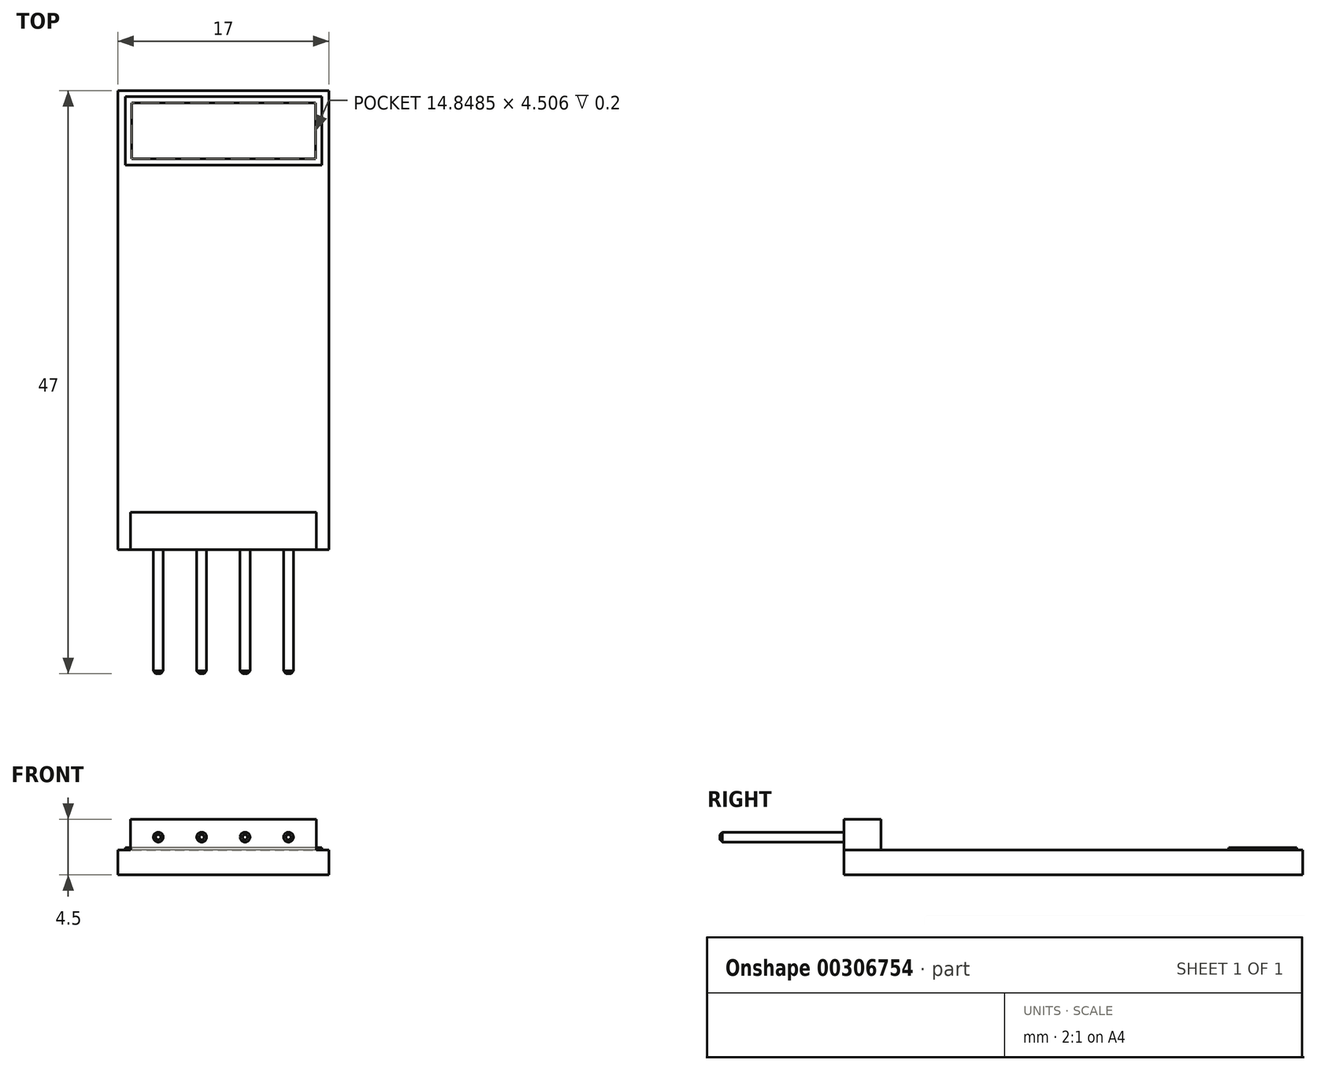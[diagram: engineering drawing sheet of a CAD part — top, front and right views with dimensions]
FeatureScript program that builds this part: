
annotation { "Feature Type Name" : "Feature", "Feature Type Description" : "" }
export const myFeature = defineFeature(function(context is Context, id is Id, definition is map)
    precondition{}
    {
        {
            var Q0;
            Q0=qCreatedBy(makeId("Top.planeOp"),FACE);
            var sketch = newSketch(context, id + "F0", { "sketchPlane" : qUnion([Q0])});
            skLineSegment(sketch, "E0.bottom", {"start": v(-8.5, 18.5) * mm, "end": v(8.5, 18.5) * mm});
            skLineSegment(sketch, "E0.top", {"start": v(-8.5, -18.5) * mm, "end": v(8.5, -18.5) * mm});
            skLineSegment(sketch, "E0.left", {"start": v(-8.5, 18.5) * mm, "end": v(-8.5, -18.5) * mm});
            skLineSegment(sketch, "E0.right", {"start": v(8.5, 18.5) * mm, "end": v(8.5, -18.5) * mm});
            skSolve(sketch);
        }
        {
            var Q0;
            Q0=makeQuery(id+"F0.imprint","IMPRINT",FACE,{"disambiguationData":[TD([[makeQuery(id+"F0.imprint","IMPRINT",EDGE,{"derivedFrom":sQuery(id+"F0.wireOp",EDGE,"E0.bottom")}),-1.0]])]});
            extrude(context, id + "F1", {"entities" : qUnion([Q0]), "depth" : 2 * mm, "symmetric" : true});
        }
        {
            var Q0;
            Q0=makeQuery(id+"F1.opExtrude","CAP_FACE",FACE,{"disambiguationData":[OSD([sQuery(id+"F0.wireOp",EDGE,"E0.bottom"),sQuery(id+"F0.wireOp",EDGE,"E0.top"),sQuery(id+"F0.wireOp",EDGE,"E0.left"),sQuery(id+"F0.wireOp",EDGE,"E0.right")])],"isStart":false});
            var sketch = newSketch(context, id + "F2", { "sketchPlane" : qUnion([Q0])});
            skLineSegment(sketch, "E1.bottom", {"start": v(-7.5, -18.5) * mm, "end": v(7.5, -18.5) * mm});
            skLineSegment(sketch, "E1.top", {"start": v(-7.5, -15.5) * mm, "end": v(7.5, -15.5) * mm});
            skLineSegment(sketch, "E1.left", {"start": v(-7.5, -18.5) * mm, "end": v(-7.5, -15.5) * mm});
            skLineSegment(sketch, "E1.right", {"start": v(7.5, -18.5) * mm, "end": v(7.5, -15.5) * mm});
            skSolve(sketch);
        }
        {
            var Q0;
            Q0=makeQuery(id+"F2.imprint","IMPRINT",FACE,{"disambiguationData":[TD([[makeQuery(id+"F2.imprint","IMPRINT",EDGE,{"derivedFrom":sQuery(id+"F2.wireOp",EDGE,"E1.bottom")}),1.0]])]});
            extrude(context, id + "F3", {"entities" : qUnion([Q0]), "operationType" : NewBodyOperationType.ADD, "depth" : 2.5 * mm});
        }
        {
            var Q0;
            Q0=makeQuery(id+"F3.boolean.opBoolean","MERGE",FACE,{"derivedFrom":[makeQuery(id+"F1.opExtrude","SWEPT_FACE",FACE,{"disambiguationData":[OSD([sQuery(id+"F0.wireOp",EDGE,"E0.top")])]}),makeQuery(id+"F3.opExtrude","SWEPT_FACE",FACE,{"disambiguationData":[OSD([sQuery(id+"F2.wireOp",EDGE,"E1.bottom")])]})]});
            var sketch = newSketch(context, id + "F4", { "sketchPlane" : qUnion([Q0])});
            skCircle(sketch, "E2", {"center": v(-5.25, 2.05) * mm, "radius": 0.4 * mm});
            skCircle(sketch, "E3.1.0.0", {"center": v(-1.75, 2.05) * mm, "radius": 0.4 * mm});
            skCircle(sketch, "E3.2.0.0", {"center": v(1.75, 2.05) * mm, "radius": 0.4 * mm});
            skCircle(sketch, "E3.3.0.0", {"center": v(5.25, 2.05) * mm, "radius": 0.4 * mm});
            skLineSegment(sketch, "E3.direction1", {"start": v(-5.25, 2.05) * mm, "end": v(-1.75, 2.05) * mm, "construction": true});
            skLineSegment(sketch, "E4", {"start": v(-5.25, 2.05) * mm, "end": v(-7.5, 2.05) * mm, "construction": true});
            skLineSegment(sketch, "E5", {"start": v(5.25, 2.05) * mm, "end": v(7.5, 2.05) * mm, "construction": true});
            skSolve(sketch);
        }
        {
            var Q0;
            Q0=makeQuery(id+"F4.imprint","IMPRINT",FACE,{"disambiguationData":[TD([[makeQuery(id+"F4.imprint","IMPRINT",EDGE,{"derivedFrom":sQuery(id+"F4.wireOp",EDGE,"E2")}),1.0]])]});
            var Q1;
            Q1=makeQuery(id+"F4.imprint","IMPRINT",FACE,{"disambiguationData":[TD([[makeQuery(id+"F4.imprint","IMPRINT",EDGE,{"derivedFrom":sQuery(id+"F4.wireOp",EDGE,"E3.1.0.0")}),1.0]])]});
            var Q2;
            Q2=makeQuery(id+"F4.imprint","IMPRINT",FACE,{"disambiguationData":[TD([[makeQuery(id+"F4.imprint","IMPRINT",EDGE,{"derivedFrom":sQuery(id+"F4.wireOp",EDGE,"E3.2.0.0")}),1.0]])]});
            var Q3;
            Q3=makeQuery(id+"F4.imprint","IMPRINT",FACE,{"disambiguationData":[TD([[makeQuery(id+"F4.imprint","IMPRINT",EDGE,{"derivedFrom":sQuery(id+"F4.wireOp",EDGE,"E3.3.0.0")}),1.0]])]});
            extrude(context, id + "F5", {"entities" : qUnion([Q0, Q1, Q2, Q3]), "operationType" : NewBodyOperationType.ADD, "depth" : 10 * mm});
        }
        {
            var Q0;
            Q0=makeQuery(id+"F5.opExtrude","CAP_EDGE",EDGE,{"disambiguationData":[OSD([sQuery(id+"F4.wireOp",EDGE,"E2")])],"isStart":false});
            var Q1;
            Q1=makeQuery(id+"F5.opExtrude","CAP_EDGE",EDGE,{"disambiguationData":[OSD([sQuery(id+"F4.wireOp",EDGE,"E3.1.0.0")])],"isStart":false});
            var Q2;
            Q2=makeQuery(id+"F5.opExtrude","CAP_EDGE",EDGE,{"disambiguationData":[OSD([sQuery(id+"F4.wireOp",EDGE,"E3.2.0.0")])],"isStart":false});
            var Q3;
            Q3=makeQuery(id+"F5.opExtrude","CAP_EDGE",EDGE,{"disambiguationData":[OSD([sQuery(id+"F4.wireOp",EDGE,"E3.3.0.0")])],"isStart":false});
            chamfer(context, id + "F6", {"entities" : qUnion([Q0, Q1, Q2, Q3]), "width" : 0.2 * mm, "tangentPropagation" : true});
        }
        {
            var Q0;
            Q0=makeQuery(id+"F1.opExtrude","CAP_FACE",FACE,{"disambiguationData":[OSD([sQuery(id+"F0.wireOp",EDGE,"E0.bottom"),sQuery(id+"F0.wireOp",EDGE,"E0.top"),sQuery(id+"F0.wireOp",EDGE,"E0.left"),sQuery(id+"F0.wireOp",EDGE,"E0.right")])],"isStart":false});
            var sketch = newSketch(context, id + "F7", { "sketchPlane" : qUnion([Q0])});
            skLineSegment(sketch, "E6.bottom", {"start": v(7.95, 18.02) * mm, "end": v(-7.9, 18.02) * mm});
            skLineSegment(sketch, "E6.top", {"start": v(7.95, 12.51) * mm, "end": v(-7.9, 12.51) * mm});
            skLineSegment(sketch, "E6.left", {"start": v(7.95, 18.02) * mm, "end": v(7.95, 12.51) * mm});
            skLineSegment(sketch, "E6.right", {"start": v(-7.9, 18.02) * mm, "end": v(-7.9, 12.51) * mm});
            skLineSegment(sketch, "E7.0", {"start": v(7.45, 17.52) * mm, "end": v(7.45, 13.01) * mm});
            skLineSegment(sketch, "E7.1", {"start": v(7.45, 17.52) * mm, "end": v(-7.4, 17.52) * mm});
            skLineSegment(sketch, "E7.2", {"start": v(-7.4, 17.52) * mm, "end": v(-7.4, 13.01) * mm});
            skLineSegment(sketch, "E7.3", {"start": v(7.45, 13.01) * mm, "end": v(-7.4, 13.01) * mm});
            skSolve(sketch);
        }
        {
            var Q0;
            Q0=makeQuery(id+"F7.imprint","IMPRINT",FACE,{"disambiguationData":[TD([[makeQuery(id+"F7.imprint","IMPRINT",EDGE,{"derivedFrom":sQuery(id+"F7.wireOp",EDGE,"E6.bottom")}),1.0]])]});
            extrude(context, id + "F8", {"entities" : qUnion([Q0]), "operationType" : NewBodyOperationType.ADD, "depth" : 0.2 * mm});
        }
    });
